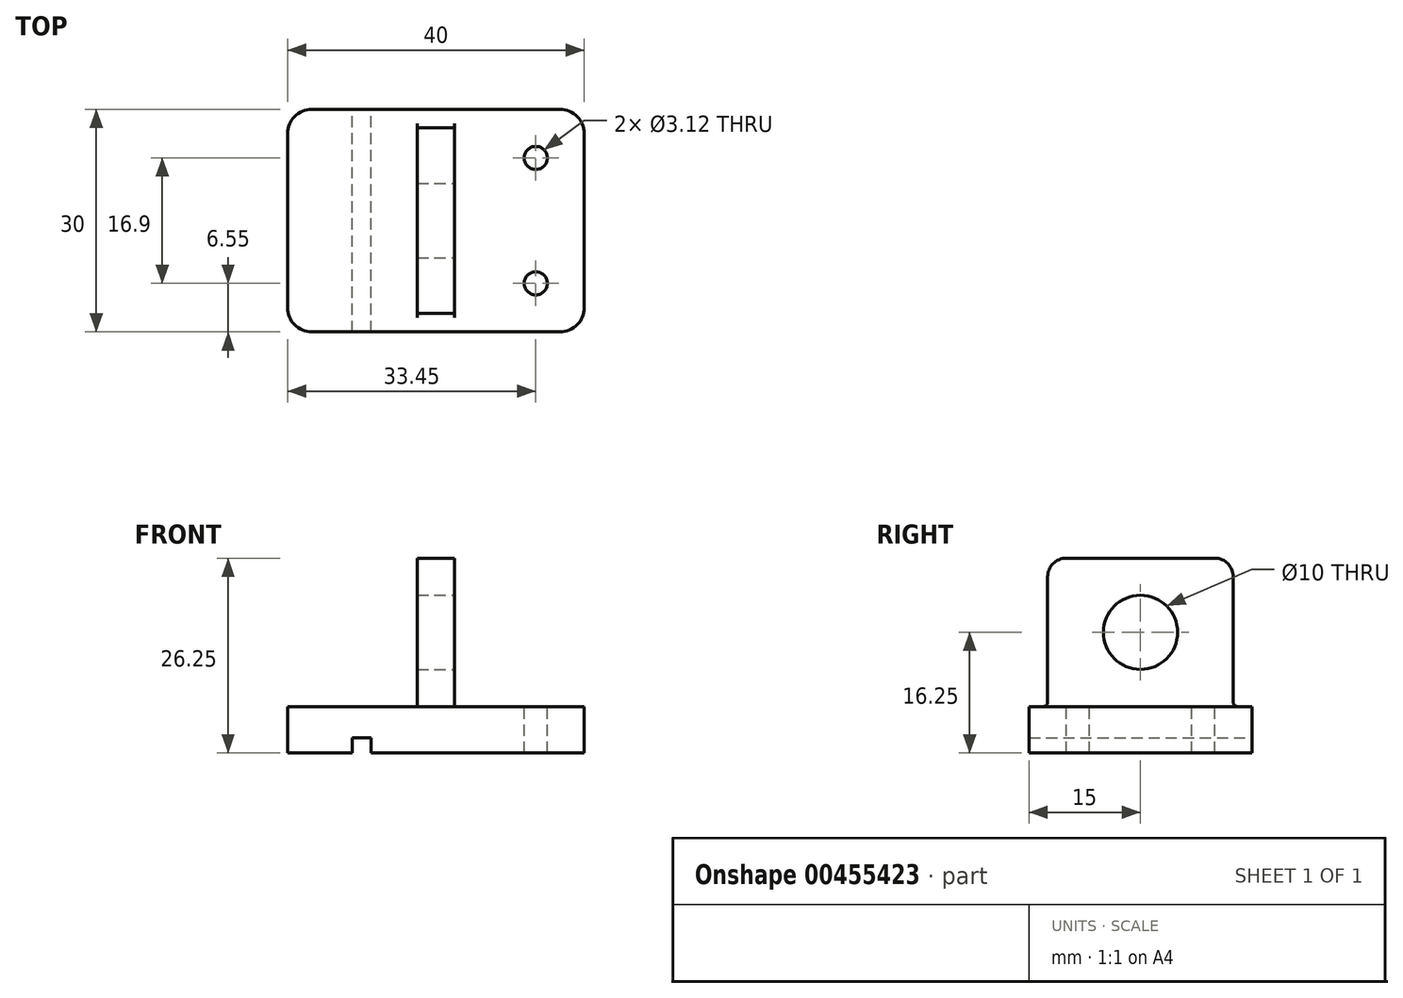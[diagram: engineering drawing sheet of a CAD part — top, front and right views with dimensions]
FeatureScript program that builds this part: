
annotation { "Feature Type Name" : "Feature", "Feature Type Description" : "" }
export const myFeature = defineFeature(function(context is Context, id is Id, definition is map)
    precondition{}
    {
        {
            var Q0;
            Q0=qCreatedBy(makeId("Top.planeOp"),FACE);
            var sketch = newSketch(context, id + "F0", { "sketchPlane" : qUnion([Q0])});
            skLineSegment(sketch, "E0.bottom", {"start": v(-16.73, 15) * mm, "end": v(16.72, 15) * mm});
            skLineSegment(sketch, "E0.top", {"start": v(-16.73, -15) * mm, "end": v(16.72, -15) * mm});
            skLineSegment(sketch, "E0.left", {"start": v(-20, 11.72) * mm, "end": v(-20, -11.73) * mm});
            skLineSegment(sketch, "E0.right", {"start": v(20, 11.72) * mm, "end": v(20, -11.73) * mm});
            skPoint(sketch, "E0.middle", {"position": v(0, 0) * mm});
            skArc(sketch, "E1", {"start": v(-20, -11.72) * mm, "mid": v(-19.04, -14.04) * mm, "end": v(-16.73, -15) * mm});
            skPoint(sketch, "E2.orphan", {"position": v(-20, -15) * mm});
            skArc(sketch, "E3", {"start": v(16.72, -15) * mm, "mid": v(19.04, -14.04) * mm, "end": v(20, -11.73) * mm});
            skArc(sketch, "E4", {"start": v(20, 11.72) * mm, "mid": v(19.04, 14.04) * mm, "end": v(16.72, 15) * mm});
            skArc(sketch, "E5", {"start": v(-16.73, 15) * mm, "mid": v(-19.04, 14.04) * mm, "end": v(-20, 11.72) * mm});
            skPoint(sketch, "E6.orphan", {"position": v(-20, 15) * mm});
            skPoint(sketch, "E7.orphan", {"position": v(20, 15) * mm});
            skPoint(sketch, "E8.orphan", {"position": v(20, -15) * mm});
            skLineSegment(sketch, "E9.bottom", {"start": v(20, 15) * mm, "end": v(13.45, 15) * mm});
            skLineSegment(sketch, "E9.top", {"start": v(20, -8.45) * mm, "end": v(13.45, -8.45) * mm, "construction": true});
            skLineSegment(sketch, "E9.left", {"start": v(20, 15) * mm, "end": v(20, -8.45) * mm});
            skLineSegment(sketch, "E9.right", {"start": v(13.45, 15) * mm, "end": v(13.45, -8.45) * mm, "construction": true});
            skCircle(sketch, "E10", {"center": v(13.45, -8.45) * mm, "radius": 1.56 * mm});
            skLineSegment(sketch, "E11.bottom", {"start": v(20, -15) * mm, "end": v(13.45, -15) * mm, "construction": true});
            skLineSegment(sketch, "E11.top", {"start": v(20, 8.45) * mm, "end": v(13.45, 8.45) * mm, "construction": true});
            skLineSegment(sketch, "E11.left", {"start": v(20, -15) * mm, "end": v(20, 8.45) * mm, "construction": true});
            skLineSegment(sketch, "E11.right", {"start": v(13.45, -15) * mm, "end": v(13.45, 8.45) * mm, "construction": true});
            skCircle(sketch, "E12", {"center": v(13.45, 8.45) * mm, "radius": 1.56 * mm});
            skLineSegment(sketch, "E13.bottom", {"start": v(-2.5, 12.5) * mm, "end": v(2.5, 12.5) * mm});
            skLineSegment(sketch, "E13.top", {"start": v(-2.5, -12.5) * mm, "end": v(2.5, -12.5) * mm});
            skLineSegment(sketch, "E13.left", {"start": v(-2.5, 12.5) * mm, "end": v(-2.5, -12.5) * mm});
            skLineSegment(sketch, "E13.right", {"start": v(2.5, 12.5) * mm, "end": v(2.5, -12.5) * mm});
            skSolve(sketch);
        }
        {
            var Q0;
            Q0=qCreatedBy(makeId("Front.planeOp"),FACE);
            var sketch = newSketch(context, id + "F1", { "sketchPlane" : qUnion([Q0])});
            skLineSegment(sketch, "E14.bottom", {"start": v(0, 0) * mm, "end": v(2.45, 0) * mm});
            skLineSegment(sketch, "E14.top", {"start": v(0, 20) * mm, "end": v(2.45, 20) * mm});
            skLineSegment(sketch, "E14.right", {"start": v(2.45, 0) * mm, "end": v(2.45, 20) * mm});
            skLineSegment(sketch, "E15.bottom", {"start": v(0, 0) * mm, "end": v(-2.45, 0) * mm});
            skLineSegment(sketch, "E15.top", {"start": v(0, 20) * mm, "end": v(-2.45, 20) * mm});
            skLineSegment(sketch, "E15.right", {"start": v(-2.45, 0) * mm, "end": v(-2.45, 20) * mm});
            skLineSegment(sketch, "E16", {"start": v(20.02, 0) * mm, "end": v(-19.98, 0) * mm});
            skPoint(sketch, "E16.endSnap0", {"position": v(-1.22, 0) * mm});
            skSolve(sketch);
        }
        {
            var Q0;
            {var subQ1=sQuery(id+"F0.wireOp",EDGE,"E0.bottom");Q0=makeQuery(id+"F0.imprint","IMPRINT",FACE,{"disambiguationData":[TD([[makeQuery(id+"F0.imprint","IMPRINT",EDGE,{"derivedFrom":subQ1}),-1.0]])]});}
            var Q1;
            Q1=makeQuery(id+"F0.imprint","IMPRINT",FACE,{"disambiguationData":[TD([[makeQuery(id+"F0.imprint","IMPRINT",EDGE,{"derivedFrom":sQuery(id+"F0.wireOp",EDGE,"E13.bottom")}),-1.0]])]});
            extrude(context, id + "F2", {"entities" : qUnion([Q0, Q1]), "oppositeDirection" : true, "depth" : 6.25 * mm});
        }
        {
            var Q0;
            Q0=makeQuery(id+"F0.imprint","IMPRINT",FACE,{"disambiguationData":[TD([[makeQuery(id+"F0.imprint","IMPRINT",EDGE,{"derivedFrom":sQuery(id+"F0.wireOp",EDGE,"E13.bottom")}),-1.0]])]});
            extrude(context, id + "F3", {"entities" : qUnion([Q0]), "operationType" : NewBodyOperationType.ADD, "depth" : 20 * mm});
        }
        {
            var Q0;
            Q0=makeQuery(id+"F3.opExtrude","SWEPT_FACE",FACE,{"disambiguationData":[OSD([sQuery(id+"F0.wireOp",EDGE,"E13.right")])]});
            var sketch = newSketch(context, id + "F4", { "sketchPlane" : qUnion([Q0])});
            skArc(sketch, "E17", {"start": v(-13.1, 0) * mm, "mid": v(-12.68, 0.18) * mm, "end": v(-12.5, 0.6) * mm});
            skLineSegment(sketch, "E18", {"start": v(-12.5, 0) * mm, "end": v(-12.5, 0.6) * mm});
            skLineSegment(sketch, "E19", {"start": v(-12.5, 0) * mm, "end": v(-13.1, 0) * mm});
            skLineSegment(sketch, "E20", {"start": v(12.5, 0) * mm, "end": v(13.1, 0) * mm});
            skArc(sketch, "E21", {"start": v(12.5, 0.6) * mm, "mid": v(12.68, 0.18) * mm, "end": v(13.1, 0) * mm});
            skLineSegment(sketch, "E22", {"start": v(12.5, 0) * mm, "end": v(12.5, 0.6) * mm});
            skSolve(sketch);
        }
        {
            var Q0;
            {var subQ3=sQuery(id+"F4.wireOp",EDGE,"E18");Q0=makeQuery(id+"F4.imprint","IMPRINT",FACE,{"disambiguationData":[TD([[makeQuery(id+"F4.imprint","IMPRINT",EDGE,{"derivedFrom":subQ3}),1.0]])]});}
            var sketch = newSketch(context, id + "F5", { "sketchPlane" : qUnion([Q0])});
            skCircle(sketch, "E23", {"center": v(0, 10) * mm, "radius": 5 * mm});
            skArc(sketch, "E24", {"start": v(-10, 20) * mm, "mid": v(-11.77, 15.73) * mm, "end": v(-7.5, 17.5) * mm});
            skArc(sketch, "E25", {"start": v(7.5, 17.5) * mm, "mid": v(11.77, 15.73) * mm, "end": v(10, 20) * mm});
            skLineSegment(sketch, "E26.bottom", {"start": v(-7.5, 20) * mm, "end": v(7.5, 20) * mm});
            skLineSegment(sketch, "E26.top", {"start": v(-7.5, 0) * mm, "end": v(7.5, 0) * mm});
            skLineSegment(sketch, "E26.left", {"start": v(-7.5, 20) * mm, "end": v(-7.5, 0) * mm});
            skLineSegment(sketch, "E26.right", {"start": v(7.5, 20) * mm, "end": v(7.5, 0) * mm});
            skPoint(sketch, "E27", {"position": v(-10, 20) * mm});
            skPoint(sketch, "E28", {"position": v(-7.5, 17.5) * mm});
            skLineSegment(sketch, "E29", {"start": v(-7.5, 20) * mm, "end": v(-10, 20) * mm});
            skLineSegment(sketch, "E30", {"start": v(-7.5, 17.5) * mm, "end": v(-7.5, 20) * mm});
            skLineSegment(sketch, "E31", {"start": v(10, 20) * mm, "end": v(12.5, 20) * mm});
            skLineSegment(sketch, "E32", {"start": v(12.5, 20) * mm, "end": v(12.5, 17.5) * mm});
            skSolve(sketch);
        }
        {
            var Q0;
            Q0=makeQuery(id+"F5.imprint","IMPRINT",FACE,{"disambiguationData":[TD([[makeQuery(id+"F5.imprint","IMPRINT",EDGE,{"derivedFrom":sQuery(id+"F5.wireOp",EDGE,"E24")}),-1.0]])]});
            var Q1;
            Q1=sQuery(id+"F5.wireOp",EDGE,"E24");
            var Q2;
            Q2=sQuery(id+"F5.wireOp",EDGE,"E29");
            var Q3;
            Q3=sQuery(id+"F5.wireOp",EDGE,"E30");
            extrude(context, id + "F6", {"entities" : qUnion([Q0]), "operationType" : NewBodyOperationType.REMOVE, "surfaceEntities" : qUnion([Q1, Q2, Q3]), "oppositeDirection" : true, "depth" : 5.8 * mm});
        }
        {
            var Q0;
            Q0=makeQuery(id+"F4.imprint","IMPRINT",FACE,{"disambiguationData":[TD([[makeQuery(id+"F4.imprint","IMPRINT",EDGE,{"derivedFrom":sQuery(id+"F4.wireOp",EDGE,"E17")}),-1.0]])]});
            extrude(context, id + "F7", {"entities" : qUnion([Q0]), "operationType" : NewBodyOperationType.ADD, "oppositeDirection" : true, "depth" : 5 * mm});
        }
        {
            var Q0;
            Q0=makeQuery(id+"F5.imprint","IMPRINT",FACE,{"disambiguationData":[TD([[makeQuery(id+"F5.imprint","IMPRINT",EDGE,{"derivedFrom":sQuery(id+"F5.wireOp",EDGE,"E23")}),1.0]])]});
            extrude(context, id + "F8", {"entities" : qUnion([Q0]), "operationType" : NewBodyOperationType.REMOVE, "oppositeDirection" : true, "depth" : 5 * mm});
        }
        {
            var Q0;
            {var subQ0=sQuery(id+"F5.wireOp",EDGE,"E31");var subQ1=sQuery(id+"F5.wireOp",EDGE,"E25");var subQ2=sQuery(id+"F0.wireOp",EDGE,"E13.right");var subQ3=makeQuery(id+"F5.imprint","INTERSECT",VERTEX,{"derivedFrom":[makeQuery(id+"F4.imprint","IMPRINT",EDGE,{"derivedFrom":makeQuery(id+"F3.opExtrude","CAP_EDGE",EDGE,{"disambiguationData":[OSD([subQ2])],"isStart":false})}),subQ1,subQ0]});Q0=makeQuery(id+"F5.imprint","IMPRINT",FACE,{"disambiguationData":[TD([[makeQuery(id+"F5.imprint","IMPRINT",EDGE,{"disambiguationData":[TD([[subQ3,1.0]])],"derivedFrom":subQ0}),1.0]])]});}
            extrude(context, id + "F9", {"entities" : qUnion([Q0]), "operationType" : NewBodyOperationType.REMOVE, "oppositeDirection" : true, "depth" : 5 * mm});
        }
        {
            var Q0;
            Q0=makeQuery(id+"F4.imprint","IMPRINT",FACE,{"disambiguationData":[TD([[makeQuery(id+"F4.imprint","IMPRINT",EDGE,{"derivedFrom":sQuery(id+"F4.wireOp",EDGE,"E20")}),1.0]])]});
            extrude(context, id + "F10", {"entities" : qUnion([Q0]), "operationType" : NewBodyOperationType.ADD, "oppositeDirection" : true, "depth" : 5 * mm});
        }
        {
            var Q0;
            Q0=makeQuery(id+"F2.opExtrude","CAP_FACE",FACE,{"disambiguationData":[OSD([sQuery(id+"F0.wireOp",EDGE,"E0.bottom"),sQuery(id+"F0.wireOp",EDGE,"E0.top"),sQuery(id+"F0.wireOp",EDGE,"E0.left"),sQuery(id+"F0.wireOp",EDGE,"E0.right"),sQuery(id+"F0.wireOp",EDGE,"E1"),sQuery(id+"F0.wireOp",EDGE,"E3"),sQuery(id+"F0.wireOp",EDGE,"E4"),sQuery(id+"F0.wireOp",EDGE,"E5"),sQuery(id+"F0.wireOp",EDGE,"E9.bottom"),sQuery(id+"F0.wireOp",EDGE,"E9.left"),sQuery(id+"F0.wireOp",EDGE,"E10"),sQuery(id+"F0.wireOp",EDGE,"E12")])],"isStart":false});
            var sketch = newSketch(context, id + "F11", { "sketchPlane" : qUnion([Q0])});
            skLineSegment(sketch, "E33", {"start": v(-20, 0) * mm, "end": v(-10, 0) * mm, "construction": true});
            skLineSegment(sketch, "E34.bottom", {"start": v(-11.25, 15) * mm, "end": v(-8.75, 15) * mm});
            skLineSegment(sketch, "E34.top", {"start": v(-11.25, -15) * mm, "end": v(-8.75, -15) * mm});
            skLineSegment(sketch, "E34.left", {"start": v(-11.25, 15) * mm, "end": v(-11.25, -15) * mm});
            skLineSegment(sketch, "E34.right", {"start": v(-8.75, 15) * mm, "end": v(-8.75, -15) * mm});
            skPoint(sketch, "E34.middle", {"position": v(-10, 0) * mm});
            skSolve(sketch);
        }
        {
            var Q0;
            Q0=makeQuery(id+"F11.imprint","IMPRINT",FACE,{"disambiguationData":[TD([[makeQuery(id+"F11.imprint","IMPRINT",EDGE,{"derivedFrom":sQuery(id+"F11.wireOp",EDGE,"E34.bottom")}),-1.0]])]});
            extrude(context, id + "F12", {"entities" : qUnion([Q0]), "operationType" : NewBodyOperationType.REMOVE, "oppositeDirection" : true, "depth" : 2 * mm});
        }
    });
